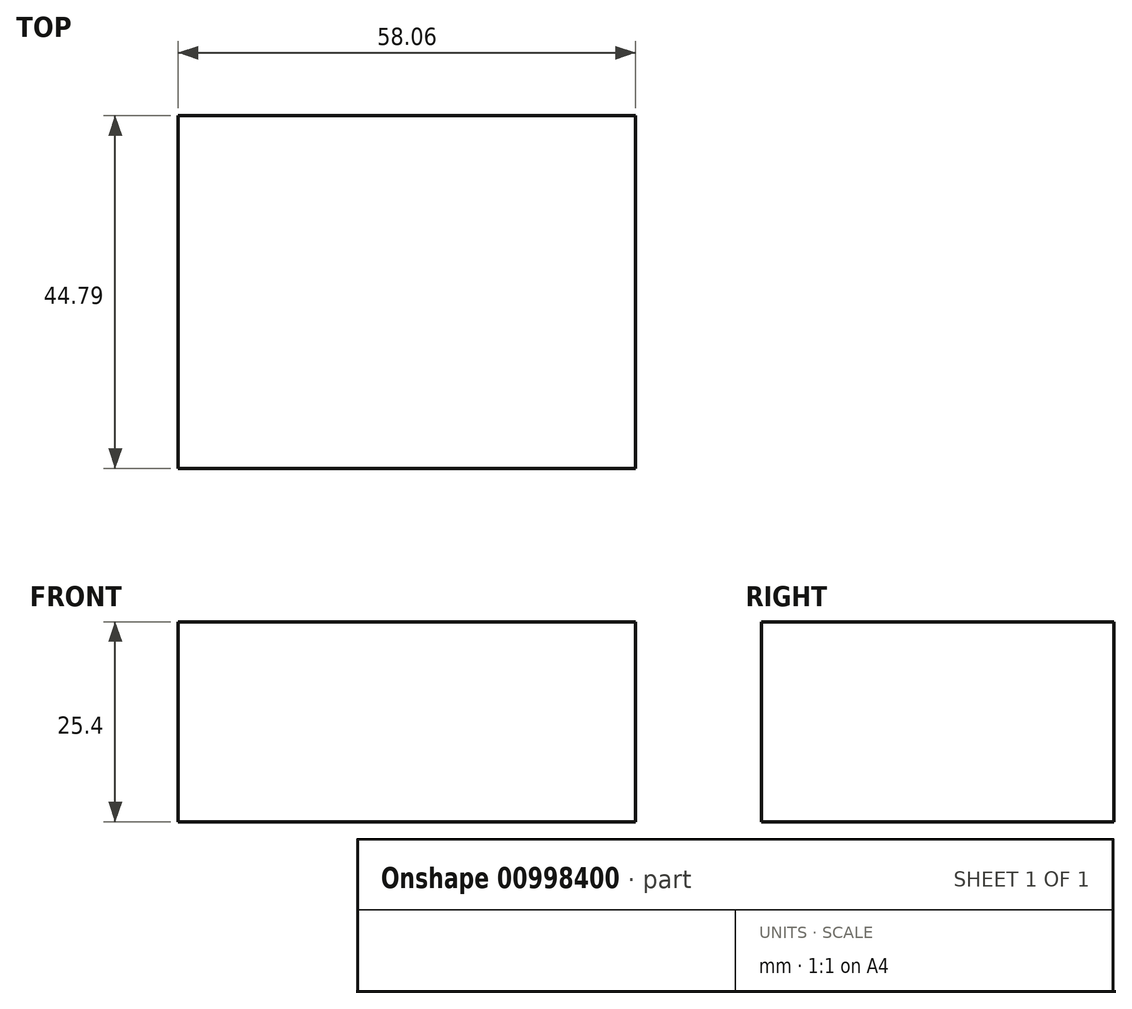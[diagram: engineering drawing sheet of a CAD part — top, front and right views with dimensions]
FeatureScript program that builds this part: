
annotation { "Feature Type Name" : "Feature", "Feature Type Description" : "" }
export const myFeature = defineFeature(function(context is Context, id is Id, definition is map)
    precondition{}
    {
        {
            var Q0;
            Q0=qCreatedBy(makeId("Top.planeOp"),FACE);
            var sketch = newSketch(context, id + "F0", { "sketchPlane" : qUnion([Q0])});
            skLineSegment(sketch, "E0.bottom", {"start": v(0, 0) * mm, "end": v(58.06, 0) * mm});
            skLineSegment(sketch, "E0.top", {"start": v(0, -44.79) * mm, "end": v(58.06, -44.79) * mm});
            skLineSegment(sketch, "E0.left", {"start": v(0, 0) * mm, "end": v(0, -44.79) * mm});
            skLineSegment(sketch, "E0.right", {"start": v(58.06, 0) * mm, "end": v(58.06, -44.79) * mm});
            skSolve(sketch);
        }
        {
            var Q0;
            Q0=makeQuery(id+"F0.imprint","IMPRINT",FACE,{"disambiguationData":[TD([[makeQuery(id+"F0.imprint","IMPRINT",EDGE,{"derivedFrom":sQuery(id+"F0.wireOp",EDGE,"E0.bottom")}),-1.0]])]});
            extrude(context, id + "F1", {"entities" : qUnion([Q0]), "depth" : 25.4 * mm, "offsetDistance" : 25.4 * mm});
        }
    });
